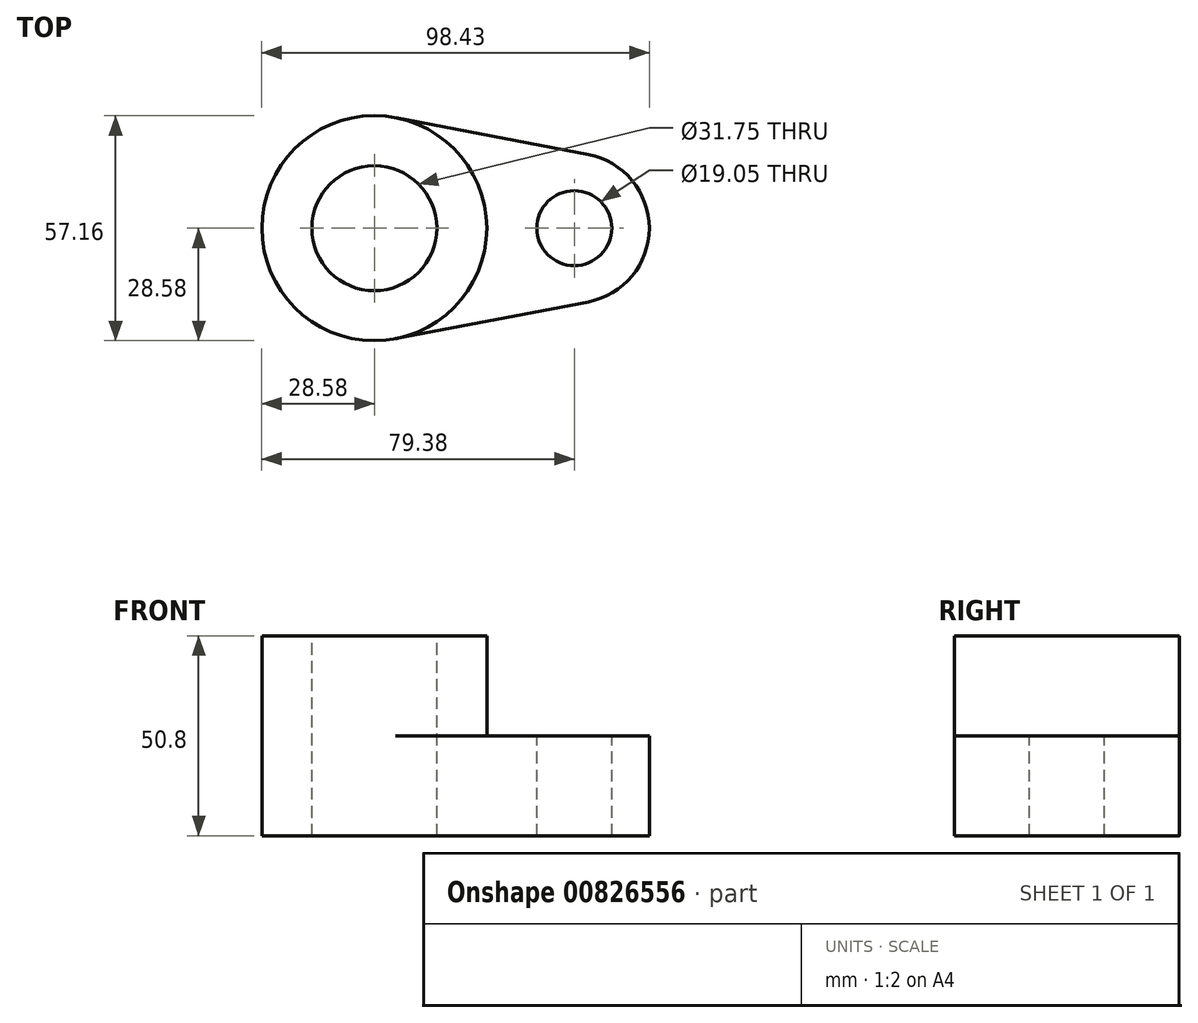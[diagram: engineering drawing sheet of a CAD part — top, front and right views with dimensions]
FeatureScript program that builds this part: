
annotation { "Feature Type Name" : "Feature", "Feature Type Description" : "" }
export const myFeature = defineFeature(function(context is Context, id is Id, definition is map)
    precondition{}
    {
        {
            var Q0;
            Q0=qCreatedBy(makeId("Top.planeOp"),FACE);
            var sketch = newSketch(context, id + "F0", { "sketchPlane" : qUnion([Q0])});
            skCircle(sketch, "E0", {"center": v(0, 0) * mm, "radius": 28.58 * mm});
            skCircle(sketch, "E1", {"center": v(0, 0) * mm, "radius": 15.88 * mm});
            skCircle(sketch, "E2", {"center": v(50.8, 0) * mm, "radius": 19.05 * mm});
            skCircle(sketch, "E3", {"center": v(50.8, 0) * mm, "radius": 9.53 * mm});
            skLineSegment(sketch, "E4", {"start": v(5.36, -28.07) * mm, "end": v(54.37, -18.71) * mm});
            skLineSegment(sketch, "E5", {"start": v(5.36, 28.07) * mm, "end": v(54.37, 18.71) * mm});
            skSolve(sketch);
        }
        {
            var Q0;
            Q0=makeQuery(id+"F0.imprint","IMPRINT",FACE,{"disambiguationData":[TD([[makeQuery(id+"F0.imprint","IMPRINT",EDGE,{"derivedFrom":sQuery(id+"F0.wireOp",EDGE,"E1")}),-1.0]])]});
            var Q1;
            Q1=makeQuery(id+"F0.imprint","IMPRINT",FACE,{"disambiguationData":[TD([[makeQuery(id+"F0.imprint","IMPRINT",EDGE,{"derivedFrom":sQuery(id+"F0.wireOp",EDGE,"E3")}),-1.0]])]});
            var Q2;
            {var subQ0=sQuery(id+"F0.wireOp",EDGE,"E4");Q2=makeQuery(id+"F0.imprint","IMPRINT",FACE,{"disambiguationData":[TD([[makeQuery(id+"F0.imprint","IMPRINT",EDGE,{"derivedFrom":subQ0}),1.0]])]});}
            extrude(context, id + "F1", {"entities" : qUnion([Q0, Q1, Q2]), "oppositeDirection" : true, "depth" : 25.4 * mm, "offsetDistance" : 25.4 * mm});
        }
        {
            var Q0;
            Q0=makeQuery(id+"F0.imprint","IMPRINT",FACE,{"disambiguationData":[TD([[makeQuery(id+"F0.imprint","IMPRINT",EDGE,{"derivedFrom":sQuery(id+"F0.wireOp",EDGE,"E1")}),-1.0]])]});
            extrude(context, id + "F2", {"entities" : qUnion([Q0]), "operationType" : NewBodyOperationType.ADD, "depth" : 25.4 * mm, "offsetDistance" : 25.4 * mm});
        }
    });
